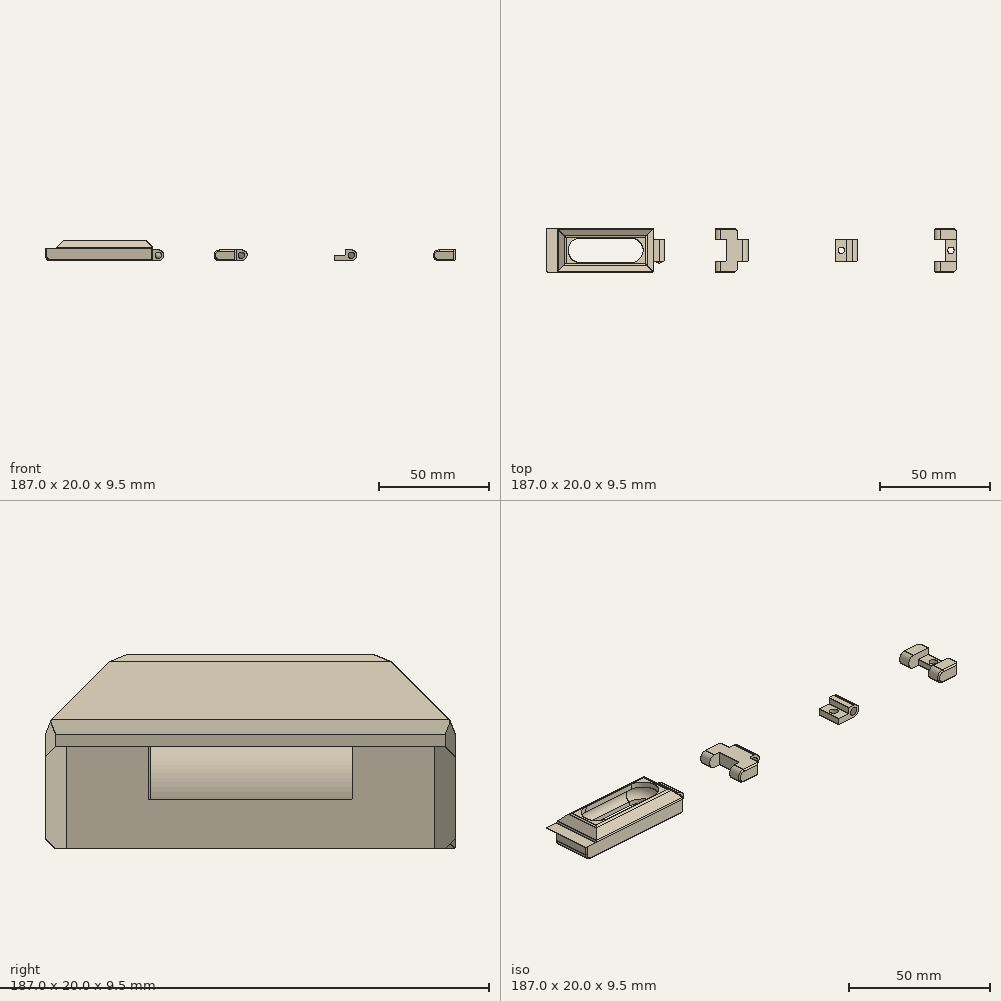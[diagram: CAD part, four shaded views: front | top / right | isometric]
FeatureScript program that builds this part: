
annotation { "Feature Type Name" : "Feature", "Feature Type Description" : "" }
export const myFeature = defineFeature(function(context is Context, id is Id, definition is map)
    precondition{}
    {
        {
            var Q0;
            Q0=qCreatedBy(makeId("Top.planeOp"),FACE);
            var sketch = newSketch(context, id + "F0", { "sketchPlane" : qUnion([Q0])});
            skLineSegment(sketch, "E0.bottom", {"start": v(-22, 10) * mm, "end": v(0, 10) * mm});
            skLineSegment(sketch, "E0.top", {"start": v(-22, -10) * mm, "end": v(0, -10) * mm});
            skLineSegment(sketch, "E0.left", {"start": v(-22, 10) * mm, "end": v(-22, -10) * mm});
            skLineSegment(sketch, "E0.right", {"start": v(0, 10) * mm, "end": v(0, -10) * mm});
            skSolve(sketch);
        }
        {
            var Q0;
            Q0=makeQuery(id+"F0.imprint","IMPRINT",FACE,{"disambiguationData":[TD([[makeQuery(id+"F0.imprint","IMPRINT",EDGE,{"derivedFrom":sQuery(id+"F0.wireOp",EDGE,"E0.bottom")}),-1.0]])]});
            extrude(context, id + "F1", {"entities" : qUnion([Q0]), "depth" : 10 * mm, "offsetDistance" : 25 * mm});
        }
        {
            var Q0;
            Q0=qCreatedBy(makeId("Right.planeOp"),FACE);
            var sketch = newSketch(context, id + "F2", { "sketchPlane" : qUnion([Q0])});
            skLineSegment(sketch, "E1.bottom", {"start": v(-5.6, 10) * mm, "end": v(5.6, 10) * mm});
            skLineSegment(sketch, "E1.left", {"start": v(-5.6, 10) * mm, "end": v(-5.5, 7.4) * mm});
            skLineSegment(sketch, "E1.right", {"start": v(5.6, 10) * mm, "end": v(5.7, 7.4) * mm});
            skLineSegment(sketch, "E2", {"start": v(-5.5, 1.4) * mm, "end": v(5.5, 1.4) * mm});
            skArc(sketch, "E3.trimOffspring", {"start": v(5.5, 1.4) * mm, "mid": v(8.5, 4.3) * mm, "end": v(5.7, 7.4) * mm});
            skArc(sketch, "E4.trimOffspring", {"start": v(-5.5, 7.4) * mm, "mid": v(-8.5, 4.4) * mm, "end": v(-5.5, 1.4) * mm});
            skSolve(sketch);
        }
        {
            var Q0;
            Q0=makeQuery(id+"F2.imprint","IMPRINT",FACE,{"disambiguationData":[TD([[makeQuery(id+"F2.imprint","IMPRINT",EDGE,{"derivedFrom":sQuery(id+"F2.wireOp",EDGE,"E1.bottom")}),-1.0]])]});
            extrude(context, id + "F3", {"entities" : qUnion([Q0]), "operationType" : NewBodyOperationType.REMOVE, "oppositeDirection" : true, "depth" : (37 / 2 - 7) * mm, "offsetDistance" : 25 * mm});
        }
        {
            var Q0;
            Q0=makeQuery(id+"F3.boolean.opBoolean","COPY",FACE,{"derivedFrom":makeQuery(id+"F3.opExtrude","CAP_FACE",FACE,{"disambiguationData":[OSD([sQuery(id+"F2.wireOp",EDGE,"E1.bottom"),sQuery(id+"F2.wireOp",EDGE,"E1.left"),sQuery(id+"F2.wireOp",EDGE,"E1.right"),sQuery(id+"F2.wireOp",EDGE,"E2"),sQuery(id+"F2.wireOp",EDGE,"E3.trimOffspring"),sQuery(id+"F2.wireOp",EDGE,"E4.trimOffspring")])],"isStart":false})});
            var sketch = newSketch(context, id + "F4", { "sketchPlane" : qUnion([Q0])});
            skLineSegment(sketch, "E5", {"start": v(0, 0) * mm, "end": v(0, 10) * mm});
            skSolve(sketch);
        }
        {
            var Q0;
            {var subQ0=makeQuery(id+"F3.boolean.opBoolean","COPY",EDGE,{"derivedFrom":makeQuery(id+"F3.opExtrude","CAP_EDGE",EDGE,{"disambiguationData":[OSD([sQuery(id+"F2.wireOp",EDGE,"E1.right")])],"isStart":false})});Q0=makeQuery(id+"F4.imprint","IMPRINT",FACE,{"disambiguationData":[TD([[makeQuery(id+"F4.imprint","IMPRINT",EDGE,{"derivedFrom":subQ0}),-1.0]])]});}
            var Q1;
            Q1=sQuery(id+"F4.wireOp",EDGE,"E5");
            revolve(context, id + "F5", {"operationType" : NewBodyOperationType.REMOVE, "surfaceOperationType" : NewSurfaceOperationType.NEW, "entities" : qUnion([Q0]), "axis" : qUnion([Q1]), "revolveType" : RevolveType.FULL, "oppositeDirection" : true});
        }
        {
            var Q0;
            Q0=makeQuery(id+"F1.opExtrude","SWEPT_BODY",BODY,{"disambiguationData":[OSD([sQuery(id+"F0.wireOp",EDGE,"E0.bottom"),sQuery(id+"F0.wireOp",EDGE,"E0.top"),sQuery(id+"F0.wireOp",EDGE,"E0.left"),sQuery(id+"F0.wireOp",EDGE,"E0.right")])]});
            var Q1;
            Q1=qCreatedBy(makeId("Right.planeOp"),FACE);
            mirror(context, id + "F6", {"operationType" : NewBodyOperationType.ADD, "entities" : qUnion([Q0]), "mirrorPlane" : qUnion([Q1])});
        }
        {
            var Q0;
            {var subQ0=makeQuery(id+"F1.opExtrude","CAP_FACE",FACE,{"disambiguationData":[OSD([sQuery(id+"F0.wireOp",EDGE,"E0.bottom"),sQuery(id+"F0.wireOp",EDGE,"E0.top"),sQuery(id+"F0.wireOp",EDGE,"E0.left"),sQuery(id+"F0.wireOp",EDGE,"E0.right")])],"isStart":true});Q0=makeQuery(id+"F6.boolean.opBoolean","MERGE",FACE,{"derivedFrom":[subQ0,makeQuery(id+"F6.opPattern","COPY",FACE,{"derivedFrom":subQ0,"instanceName":"1"})]});}
            var sketch = newSketch(context, id + "F7", { "sketchPlane" : qUnion([Q0])});
            skCircle(sketch, "E6", {"center": v(11.6, 0) * mm, "radius": 6.9 * mm});
            skCircle(sketch, "E7", {"center": v(-11.6, 0) * mm, "radius": 6.9 * mm});
            skLineSegment(sketch, "E8.bottom", {"start": v(-11.6, -6.9) * mm, "end": v(11.6, -6.9) * mm});
            skLineSegment(sketch, "E8.top", {"start": v(-11.6, 6.9) * mm, "end": v(11.6, 6.9) * mm});
            skLineSegment(sketch, "E8.left", {"start": v(-11.6, -6.9) * mm, "end": v(-11.6, 6.9) * mm});
            skLineSegment(sketch, "E8.right", {"start": v(11.6, -6.9) * mm, "end": v(11.6, 6.9) * mm});
            skSolve(sketch);
        }
        {
            var Q0;
            {var subQ0=sQuery(id+"F7.wireOp",EDGE,"E8.left");Q0=makeQuery(id+"F7.imprint","IMPRINT",FACE,{"disambiguationData":[TD([[makeQuery(id+"F7.imprint","IMPRINT",EDGE,{"derivedFrom":subQ0}),1.0]])]});}
            var Q1;
            {var subQ0=sQuery(id+"F7.wireOp",EDGE,"E8.left");Q1=makeQuery(id+"F7.imprint","IMPRINT",FACE,{"disambiguationData":[TD([[makeQuery(id+"F7.imprint","IMPRINT",EDGE,{"derivedFrom":subQ0}),-1.0]])]});}
            var Q2;
            {var subQ1=sQuery(id+"F7.wireOp",EDGE,"E8.bottom");Q2=makeQuery(id+"F7.imprint","IMPRINT",FACE,{"disambiguationData":[TD([[makeQuery(id+"F7.imprint","IMPRINT",EDGE,{"derivedFrom":subQ1}),1.0]])]});}
            var Q3;
            {var subQ0=sQuery(id+"F7.wireOp",EDGE,"E8.right");Q3=makeQuery(id+"F7.imprint","IMPRINT",FACE,{"disambiguationData":[TD([[makeQuery(id+"F7.imprint","IMPRINT",EDGE,{"derivedFrom":subQ0}),1.0]])]});}
            var Q4;
            {var subQ0=sQuery(id+"F7.wireOp",EDGE,"E8.right");Q4=makeQuery(id+"F7.imprint","IMPRINT",FACE,{"disambiguationData":[TD([[makeQuery(id+"F7.imprint","IMPRINT",EDGE,{"derivedFrom":subQ0}),-1.0]])]});}
            extrude(context, id + "F8", {"entities" : qUnion([Q0, Q1, Q2, Q3, Q4]), "operationType" : NewBodyOperationType.REMOVE, "oppositeDirection" : true, "depth" : 3 * mm, "offsetDistance" : 25 * mm});
        }
        {
            var Q0;
            Q0=makeQuery(id+"F1.opExtrude","CAP_EDGE",EDGE,{"disambiguationData":[OSD([sQuery(id+"F0.wireOp",EDGE,"E0.left")])],"isStart":false});
            var Q1;
            {var subQ0=makeQuery(id+"F1.opExtrude","CAP_EDGE",EDGE,{"disambiguationData":[OSD([sQuery(id+"F0.wireOp",EDGE,"E0.bottom")])],"isStart":false});Q1=makeQuery(id+"F6.boolean.opBoolean","MERGE",EDGE,{"derivedFrom":[subQ0,makeQuery(id+"F6.opPattern","COPY",EDGE,{"derivedFrom":subQ0,"instanceName":"1"})]});}
            var Q2;
            {var subQ0=makeQuery(id+"F1.opExtrude","CAP_EDGE",EDGE,{"disambiguationData":[OSD([sQuery(id+"F0.wireOp",EDGE,"E0.top")])],"isStart":false});Q2=makeQuery(id+"F6.boolean.opBoolean","MERGE",EDGE,{"derivedFrom":[subQ0,makeQuery(id+"F6.opPattern","COPY",EDGE,{"derivedFrom":subQ0,"instanceName":"1"})]});}
            var Q3;
            Q3=makeQuery(id+"F6.opPattern","COPY",EDGE,{"derivedFrom":makeQuery(id+"F1.opExtrude","CAP_EDGE",EDGE,{"disambiguationData":[OSD([sQuery(id+"F0.wireOp",EDGE,"E0.left")])],"isStart":false}),"instanceName":"1"});
            chamfer(context, id + "F9", {"entities" : qUnion([Q0, Q1, Q2, Q3]), "width" : 4 * mm, "tangentPropagation" : true});
        }
        {
            var Q0;
            {var subQ0=sQuery(id+"F0.wireOp",EDGE,"E0.bottom");var subQ1=makeQuery(id+"F1.opExtrude","CAP_FACE",FACE,{"disambiguationData":[OSD([subQ0,sQuery(id+"F0.wireOp",EDGE,"E0.top"),sQuery(id+"F0.wireOp",EDGE,"E0.left"),sQuery(id+"F0.wireOp",EDGE,"E0.right")])],"isStart":false});var subQ2=makeQuery(id+"F1.opExtrude","CAP_EDGE",EDGE,{"disambiguationData":[OSD([subQ0])],"isStart":false});Q0=makeQuery(id+"F9.opChamfer","BLEND_EDGE",EDGE,{"blendedFrom":[makeQuery(id+"F6.boolean.opBoolean","MERGE",EDGE,{"derivedFrom":[subQ2,makeQuery(id+"F6.opPattern","COPY",EDGE,{"derivedFrom":subQ2,"instanceName":"1"})]}),makeQuery(id+"F6.boolean.opBoolean","MERGE",FACE,{"derivedFrom":[subQ1,makeQuery(id+"F6.opPattern","COPY",FACE,{"derivedFrom":subQ1,"instanceName":"1"})]})],"blendedInto":[makeQuery(id+"F6.boolean.opBoolean","MERGE",FACE,{"derivedFrom":[subQ1,makeQuery(id+"F6.opPattern","COPY",FACE,{"derivedFrom":subQ1,"instanceName":"1"})]})]});}
            var Q1;
            {var subQ0=sQuery(id+"F0.wireOp",EDGE,"E0.left");var subQ1=makeQuery(id+"F1.opExtrude","CAP_FACE",FACE,{"disambiguationData":[OSD([sQuery(id+"F0.wireOp",EDGE,"E0.bottom"),sQuery(id+"F0.wireOp",EDGE,"E0.top"),subQ0,sQuery(id+"F0.wireOp",EDGE,"E0.right")])],"isStart":false});Q1=makeQuery(id+"F9.opChamfer","BLEND_EDGE",EDGE,{"blendedFrom":[makeQuery(id+"F1.opExtrude","CAP_EDGE",EDGE,{"disambiguationData":[OSD([subQ0])],"isStart":false}),makeQuery(id+"F6.boolean.opBoolean","MERGE",FACE,{"derivedFrom":[subQ1,makeQuery(id+"F6.opPattern","COPY",FACE,{"derivedFrom":subQ1,"instanceName":"1"})]})],"blendedInto":[makeQuery(id+"F6.boolean.opBoolean","MERGE",FACE,{"derivedFrom":[subQ1,makeQuery(id+"F6.opPattern","COPY",FACE,{"derivedFrom":subQ1,"instanceName":"1"})]})]});}
            var Q2;
            {var subQ0=sQuery(id+"F0.wireOp",EDGE,"E0.top");var subQ1=makeQuery(id+"F1.opExtrude","CAP_FACE",FACE,{"disambiguationData":[OSD([sQuery(id+"F0.wireOp",EDGE,"E0.bottom"),subQ0,sQuery(id+"F0.wireOp",EDGE,"E0.left"),sQuery(id+"F0.wireOp",EDGE,"E0.right")])],"isStart":false});var subQ2=makeQuery(id+"F1.opExtrude","CAP_EDGE",EDGE,{"disambiguationData":[OSD([subQ0])],"isStart":false});Q2=makeQuery(id+"F9.opChamfer","BLEND_EDGE",EDGE,{"blendedFrom":[makeQuery(id+"F6.boolean.opBoolean","MERGE",EDGE,{"derivedFrom":[subQ2,makeQuery(id+"F6.opPattern","COPY",EDGE,{"derivedFrom":subQ2,"instanceName":"1"})]}),makeQuery(id+"F6.boolean.opBoolean","MERGE",FACE,{"derivedFrom":[subQ1,makeQuery(id+"F6.opPattern","COPY",FACE,{"derivedFrom":subQ1,"instanceName":"1"})]})],"blendedInto":[makeQuery(id+"F6.boolean.opBoolean","MERGE",FACE,{"derivedFrom":[subQ1,makeQuery(id+"F6.opPattern","COPY",FACE,{"derivedFrom":subQ1,"instanceName":"1"})]})]});}
            var Q3;
            {var subQ0=sQuery(id+"F0.wireOp",EDGE,"E0.left");var subQ1=makeQuery(id+"F1.opExtrude","CAP_FACE",FACE,{"disambiguationData":[OSD([sQuery(id+"F0.wireOp",EDGE,"E0.bottom"),sQuery(id+"F0.wireOp",EDGE,"E0.top"),subQ0,sQuery(id+"F0.wireOp",EDGE,"E0.right")])],"isStart":false});Q3=makeQuery(id+"F9.opChamfer","BLEND_EDGE",EDGE,{"blendedFrom":[makeQuery(id+"F6.opPattern","COPY",EDGE,{"derivedFrom":makeQuery(id+"F1.opExtrude","CAP_EDGE",EDGE,{"disambiguationData":[OSD([subQ0])],"isStart":false}),"instanceName":"1"}),makeQuery(id+"F6.boolean.opBoolean","MERGE",FACE,{"derivedFrom":[subQ1,makeQuery(id+"F6.opPattern","COPY",FACE,{"derivedFrom":subQ1,"instanceName":"1"})]})],"blendedInto":[makeQuery(id+"F6.boolean.opBoolean","MERGE",FACE,{"derivedFrom":[subQ1,makeQuery(id+"F6.opPattern","COPY",FACE,{"derivedFrom":subQ1,"instanceName":"1"})]})]});}
            chamfer(context, id + "F10", {"entities" : qUnion([Q0, Q1, Q2, Q3]), "width" : 3 * mm, "tangentPropagation" : true});
        }
        {
            var Q0;
            {var subQ0=sQuery(id+"F0.wireOp",EDGE,"E0.left");Q0=makeQuery(id+"F9.opChamfer","BLEND_EDGE",EDGE,{"blendedFrom":[makeQuery(id+"F1.opExtrude","CAP_EDGE",EDGE,{"disambiguationData":[OSD([subQ0])],"isStart":false}),makeQuery(id+"F1.opExtrude","SWEPT_FACE",FACE,{"disambiguationData":[OSD([subQ0])]})],"blendedInto":[makeQuery(id+"F1.opExtrude","SWEPT_FACE",FACE,{"disambiguationData":[OSD([subQ0])]})]});}
            var Q1;
            {var subQ0=sQuery(id+"F0.wireOp",EDGE,"E0.bottom");var subQ1=makeQuery(id+"F1.opExtrude","SWEPT_FACE",FACE,{"disambiguationData":[OSD([subQ0])]});var subQ2=makeQuery(id+"F1.opExtrude","CAP_EDGE",EDGE,{"disambiguationData":[OSD([subQ0])],"isStart":false});Q1=makeQuery(id+"F9.opChamfer","BLEND_EDGE",EDGE,{"blendedFrom":[makeQuery(id+"F6.boolean.opBoolean","MERGE",EDGE,{"derivedFrom":[subQ2,makeQuery(id+"F6.opPattern","COPY",EDGE,{"derivedFrom":subQ2,"instanceName":"1"})]}),makeQuery(id+"F6.boolean.opBoolean","MERGE",FACE,{"derivedFrom":[subQ1,makeQuery(id+"F6.opPattern","COPY",FACE,{"derivedFrom":subQ1,"instanceName":"1"})]})],"blendedInto":[makeQuery(id+"F6.boolean.opBoolean","MERGE",FACE,{"derivedFrom":[subQ1,makeQuery(id+"F6.opPattern","COPY",FACE,{"derivedFrom":subQ1,"instanceName":"1"})]})]});}
            var Q2;
            {var subQ0=sQuery(id+"F0.wireOp",EDGE,"E0.top");var subQ1=makeQuery(id+"F1.opExtrude","SWEPT_FACE",FACE,{"disambiguationData":[OSD([subQ0])]});var subQ2=makeQuery(id+"F1.opExtrude","CAP_EDGE",EDGE,{"disambiguationData":[OSD([subQ0])],"isStart":false});Q2=makeQuery(id+"F9.opChamfer","BLEND_EDGE",EDGE,{"blendedFrom":[makeQuery(id+"F6.boolean.opBoolean","MERGE",EDGE,{"derivedFrom":[subQ2,makeQuery(id+"F6.opPattern","COPY",EDGE,{"derivedFrom":subQ2,"instanceName":"1"})]}),makeQuery(id+"F6.boolean.opBoolean","MERGE",FACE,{"derivedFrom":[subQ1,makeQuery(id+"F6.opPattern","COPY",FACE,{"derivedFrom":subQ1,"instanceName":"1"})]})],"blendedInto":[makeQuery(id+"F6.boolean.opBoolean","MERGE",FACE,{"derivedFrom":[subQ1,makeQuery(id+"F6.opPattern","COPY",FACE,{"derivedFrom":subQ1,"instanceName":"1"})]})]});}
            var Q3;
            {var subQ0=sQuery(id+"F0.wireOp",EDGE,"E0.left");Q3=makeQuery(id+"F9.opChamfer","BLEND_EDGE",EDGE,{"blendedFrom":[makeQuery(id+"F6.opPattern","COPY",EDGE,{"derivedFrom":makeQuery(id+"F1.opExtrude","CAP_EDGE",EDGE,{"disambiguationData":[OSD([subQ0])],"isStart":false}),"instanceName":"1"}),makeQuery(id+"F6.opPattern","COPY",FACE,{"derivedFrom":makeQuery(id+"F1.opExtrude","SWEPT_FACE",FACE,{"disambiguationData":[OSD([subQ0])]}),"instanceName":"1"})],"blendedInto":[makeQuery(id+"F6.opPattern","COPY",FACE,{"derivedFrom":makeQuery(id+"F1.opExtrude","SWEPT_FACE",FACE,{"disambiguationData":[OSD([subQ0])]}),"instanceName":"1"})]});}
            chamfer(context, id + "F11", {"entities" : qUnion([Q0, Q1, Q2, Q3]), "width" : 1 * mm, "tangentPropagation" : true});
        }
        {
            var Q0;
            Q0=makeQuery(id+"F1.opExtrude","SWEPT_FACE",FACE,{"disambiguationData":[OSD([sQuery(id+"F0.wireOp",EDGE,"E0.left")])]});
            var sketch = newSketch(context, id + "F12", { "sketchPlane" : qUnion([Q0])});
            skLineSegment(sketch, "E9.bottom", {"start": v(-10, 5) * mm, "end": v(-5, 5) * mm});
            skLineSegment(sketch, "E9.top", {"start": v(-10, 0) * mm, "end": v(-5, 0) * mm});
            skLineSegment(sketch, "E9.left", {"start": v(-10, 5) * mm, "end": v(-10, 0) * mm});
            skLineSegment(sketch, "E9.right", {"start": v(-5, 5) * mm, "end": v(-5, 0) * mm});
            skLineSegment(sketch, "E10.bottom", {"start": v(10, 5) * mm, "end": v(5, 5) * mm});
            skLineSegment(sketch, "E10.top", {"start": v(10, 0) * mm, "end": v(5, 0) * mm});
            skLineSegment(sketch, "E10.left", {"start": v(10, 5) * mm, "end": v(10, 0) * mm});
            skLineSegment(sketch, "E10.right", {"start": v(5, 5) * mm, "end": v(5, 0) * mm});
            skSolve(sketch);
        }
        {
            var Q0;
            Q0=makeQuery(id+"F12.imprint","IMPRINT",FACE,{"disambiguationData":[TD([[makeQuery(id+"F12.imprint","IMPRINT",EDGE,{"derivedFrom":sQuery(id+"F12.wireOp",EDGE,"E9.bottom")}),1.0]])]});
            var Q1;
            Q1=makeQuery(id+"F12.imprint","IMPRINT",FACE,{"disambiguationData":[TD([[makeQuery(id+"F12.imprint","IMPRINT",EDGE,{"derivedFrom":sQuery(id+"F12.wireOp",EDGE,"E10.bottom")}),1.0]])]});
            extrude(context, id + "F13", {"entities" : qUnion([Q0, Q1]), "operationType" : NewBodyOperationType.ADD, "depth" : 5 * mm, "offsetDistance" : 25 * mm});
        }
        {
            var Q0;
            Q0=makeQuery(id+"F6.opPattern","COPY",FACE,{"derivedFrom":makeQuery(id+"F1.opExtrude","SWEPT_FACE",FACE,{"disambiguationData":[OSD([sQuery(id+"F0.wireOp",EDGE,"E0.left")])]}),"instanceName":"1"});
            var sketch = newSketch(context, id + "F14", { "sketchPlane" : qUnion([Q0])});
            skLineSegment(sketch, "E11.bottom", {"start": v(-5, 0) * mm, "end": v(5, 0) * mm});
            skLineSegment(sketch, "E11.top", {"start": v(-5, 5) * mm, "end": v(5, 5) * mm});
            skLineSegment(sketch, "E11.left", {"start": v(-5, 0) * mm, "end": v(-5, 5) * mm});
            skLineSegment(sketch, "E11.right", {"start": v(5, 0) * mm, "end": v(5, 5) * mm});
            skSolve(sketch);
        }
        {
            var Q0;
            Q0=makeQuery(id+"F14.imprint","IMPRINT",FACE,{"disambiguationData":[TD([[makeQuery(id+"F14.imprint","IMPRINT",EDGE,{"derivedFrom":sQuery(id+"F14.wireOp",EDGE,"E11.bottom")}),-1.0]])]});
            extrude(context, id + "F15", {"entities" : qUnion([Q0]), "operationType" : NewBodyOperationType.ADD, "depth" : 5 * mm, "offsetDistance" : 25 * mm});
        }
        {
            var Q0;
            Q0=makeQuery(id+"F13.opExtrude","CAP_EDGE",EDGE,{"disambiguationData":[OSD([sQuery(id+"F12.wireOp",EDGE,"E9.bottom")])],"isStart":false});
            var Q1;
            Q1=makeQuery(id+"F13.opExtrude","CAP_EDGE",EDGE,{"disambiguationData":[OSD([sQuery(id+"F12.wireOp",EDGE,"E9.top")])],"isStart":false});
            var Q2;
            Q2=makeQuery(id+"F13.opExtrude","CAP_EDGE",EDGE,{"disambiguationData":[OSD([sQuery(id+"F12.wireOp",EDGE,"E10.bottom")])],"isStart":false});
            var Q3;
            Q3=makeQuery(id+"F13.opExtrude","CAP_EDGE",EDGE,{"disambiguationData":[OSD([sQuery(id+"F12.wireOp",EDGE,"E10.top")])],"isStart":false});
            var Q4;
            Q4=makeQuery(id+"F15.opExtrude","CAP_EDGE",EDGE,{"disambiguationData":[OSD([sQuery(id+"F14.wireOp",EDGE,"E11.top")])],"isStart":false});
            var Q5;
            Q5=makeQuery(id+"F15.opExtrude","CAP_EDGE",EDGE,{"disambiguationData":[OSD([sQuery(id+"F14.wireOp",EDGE,"E11.bottom")])],"isStart":false});
            fillet(context, id + "F16", {"entities" : qUnion([Q0, Q1, Q2, Q3, Q4, Q5]), "radius" : 2.5 * mm, "tangentPropagation" : true, "allowEdgeOverflow" : false});
        }
        {
            var Q0;
            Q0=qCreatedBy(makeId("Top.planeOp"),FACE);
            cPlane(context, id + "F17", {"entities" : qUnion([Q0]), "cplaneType" : CPlaneType.OFFSET, "offset" : 10 * mm, "width" : 150 * mm, "height" : 150 * mm});
        }
        {
            var Q0;
            Q0=qCreatedBy(id+"F17.planeOp",FACE);
            var sketch = newSketch(context, id + "F18", { "sketchPlane" : qUnion([Q0])});
            skLineSegment(sketch, "E12.bottom", {"start": v(22.66, 7.24) * mm, "end": v(-22.46, 7.24) * mm});
            skLineSegment(sketch, "E12.top", {"start": v(22.66, -7.34) * mm, "end": v(-22.46, -7.34) * mm});
            skLineSegment(sketch, "E12.left", {"start": v(22.66, 7.24) * mm, "end": v(22.66, -7.34) * mm});
            skLineSegment(sketch, "E12.right", {"start": v(-22.46, 7.24) * mm, "end": v(-22.46, -7.34) * mm});
            skSolve(sketch);
        }
        {
            var Q0;
            Q0=makeQuery(id+"F18.imprint","IMPRINT",FACE,{"disambiguationData":[TD([[makeQuery(id+"F18.imprint","IMPRINT",EDGE,{"derivedFrom":sQuery(id+"F18.wireOp",EDGE,"E12.bottom")}),1.0]])]});
            extrude(context, id + "F19", {"entities" : qUnion([Q0]), "operationType" : NewBodyOperationType.REMOVE, "oppositeDirection" : true, "depth" : 0.5 * mm, "offsetDistance" : 25 * mm});
        }
        {
            var Q0;
            Q0=qCreatedBy(makeId("Right.planeOp"),FACE);
            cPlane(context, id + "F20", {"entities" : qUnion([Q0]), "cplaneType" : CPlaneType.OFFSET, "offset" : 50 * mm, "width" : 150 * mm, "height" : 150 * mm});
        }
        {
            var Q0;
            Q0=qCreatedBy(id+"F20.planeOp",FACE);
            var sketch = newSketch(context, id + "F21", { "sketchPlane" : qUnion([Q0])});
            skLineSegment(sketch, "E13.bottom", {"start": v(-10, 0) * mm, "end": v(10, 0) * mm});
            skLineSegment(sketch, "E13.top", {"start": v(-10, 5) * mm, "end": v(10, 5) * mm});
            skLineSegment(sketch, "E13.left", {"start": v(-10, 0) * mm, "end": v(-10, 5) * mm});
            skLineSegment(sketch, "E13.right", {"start": v(10, 0) * mm, "end": v(10, 5) * mm});
            skSolve(sketch);
        }
        {
            var Q0;
            Q0=makeQuery(id+"F21.imprint","IMPRINT",FACE,{"disambiguationData":[TD([[makeQuery(id+"F21.imprint","IMPRINT",EDGE,{"derivedFrom":sQuery(id+"F21.wireOp",EDGE,"E13.bottom")}),1.0]])]});
            extrude(context, id + "F22", {"entities" : qUnion([Q0]), "depth" : 10 * mm, "offsetDistance" : 25 * mm});
        }
        {
            var Q0;
            Q0=makeQuery(id+"F22.opExtrude","CAP_FACE",FACE,{"disambiguationData":[OSD([sQuery(id+"F21.wireOp",EDGE,"E13.bottom"),sQuery(id+"F21.wireOp",EDGE,"E13.top"),sQuery(id+"F21.wireOp",EDGE,"E13.left"),sQuery(id+"F21.wireOp",EDGE,"E13.right")])],"isStart":false});
            var sketch = newSketch(context, id + "F23", { "sketchPlane" : qUnion([Q0])});
            skLineSegment(sketch, "E14.bottom", {"start": v(-5, 0) * mm, "end": v(5, 0) * mm});
            skLineSegment(sketch, "E14.top", {"start": v(-5, 5) * mm, "end": v(5, 5) * mm});
            skLineSegment(sketch, "E14.left", {"start": v(-5, 0) * mm, "end": v(-5, 5) * mm});
            skLineSegment(sketch, "E14.right", {"start": v(5, 0) * mm, "end": v(5, 5) * mm});
            skSolve(sketch);
        }
        {
            var Q0;
            Q0=makeQuery(id+"F23.imprint","IMPRINT",FACE,{"disambiguationData":[TD([[makeQuery(id+"F23.imprint","IMPRINT",EDGE,{"derivedFrom":sQuery(id+"F23.wireOp",EDGE,"E14.bottom")}),1.0]])]});
            extrude(context, id + "F24", {"entities" : qUnion([Q0]), "operationType" : NewBodyOperationType.ADD, "depth" : 5 * mm, "offsetDistance" : 25 * mm});
        }
        {
            var Q0;
            Q0=makeQuery(id+"F22.opExtrude","CAP_FACE",FACE,{"disambiguationData":[OSD([sQuery(id+"F21.wireOp",EDGE,"E13.bottom"),sQuery(id+"F21.wireOp",EDGE,"E13.top"),sQuery(id+"F21.wireOp",EDGE,"E13.left"),sQuery(id+"F21.wireOp",EDGE,"E13.right")])],"isStart":true});
            var sketch = newSketch(context, id + "F25", { "sketchPlane" : qUnion([Q0])});
            skLineSegment(sketch, "E15.bottom", {"start": v(-5, 0) * mm, "end": v(5, 0) * mm});
            skLineSegment(sketch, "E15.top", {"start": v(-5, 5) * mm, "end": v(5, 5) * mm});
            skLineSegment(sketch, "E15.left", {"start": v(-5, 0) * mm, "end": v(-5, 5) * mm});
            skLineSegment(sketch, "E15.right", {"start": v(5, 0) * mm, "end": v(5, 5) * mm});
            skSolve(sketch);
        }
        {
            var Q0;
            Q0=makeQuery(id+"F25.imprint","IMPRINT",FACE,{"disambiguationData":[TD([[makeQuery(id+"F25.imprint","IMPRINT",EDGE,{"derivedFrom":sQuery(id+"F25.wireOp",EDGE,"E15.bottom")}),-1.0]])]});
            extrude(context, id + "F26", {"entities" : qUnion([Q0]), "operationType" : NewBodyOperationType.REMOVE, "oppositeDirection" : true, "depth" : 5 * mm, "offsetDistance" : 25 * mm});
        }
        {
            var Q0;
            {var subQ0=sQuery(id+"F21.wireOp",EDGE,"E13.right");var subQ1=sQuery(id+"F21.wireOp",EDGE,"E13.top");Q0=makeQuery(id+"F26.boolean.opBoolean","SPLIT",EDGE,{"disambiguationData":[TD([makeQuery(id+"F22.opExtrude","SWEPT_FACE",FACE,{"disambiguationData":[OSD([subQ0])]})])],"derivedFrom":makeQuery(id+"F22.opExtrude","CAP_EDGE",EDGE,{"disambiguationData":[OSD([subQ1])],"isStart":true})});}
            var Q1;
            {var subQ0=sQuery(id+"F21.wireOp",EDGE,"E13.right");var subQ1=sQuery(id+"F21.wireOp",EDGE,"E13.bottom");Q1=makeQuery(id+"F26.boolean.opBoolean","SPLIT",EDGE,{"disambiguationData":[TD([makeQuery(id+"F22.opExtrude","SWEPT_FACE",FACE,{"disambiguationData":[OSD([subQ0])]})])],"derivedFrom":makeQuery(id+"F22.opExtrude","CAP_EDGE",EDGE,{"disambiguationData":[OSD([subQ1])],"isStart":true})});}
            var Q2;
            {var subQ0=sQuery(id+"F21.wireOp",EDGE,"E13.left");var subQ1=sQuery(id+"F21.wireOp",EDGE,"E13.top");Q2=makeQuery(id+"F26.boolean.opBoolean","SPLIT",EDGE,{"disambiguationData":[TD([makeQuery(id+"F22.opExtrude","SWEPT_FACE",FACE,{"disambiguationData":[OSD([subQ0])]})])],"derivedFrom":makeQuery(id+"F22.opExtrude","CAP_EDGE",EDGE,{"disambiguationData":[OSD([subQ1])],"isStart":true})});}
            var Q3;
            {var subQ0=sQuery(id+"F21.wireOp",EDGE,"E13.left");var subQ1=sQuery(id+"F21.wireOp",EDGE,"E13.bottom");Q3=makeQuery(id+"F26.boolean.opBoolean","SPLIT",EDGE,{"disambiguationData":[TD([makeQuery(id+"F22.opExtrude","SWEPT_FACE",FACE,{"disambiguationData":[OSD([subQ0])]})])],"derivedFrom":makeQuery(id+"F22.opExtrude","CAP_EDGE",EDGE,{"disambiguationData":[OSD([subQ1])],"isStart":true})});}
            var Q4;
            Q4=makeQuery(id+"F24.opExtrude","CAP_EDGE",EDGE,{"disambiguationData":[OSD([sQuery(id+"F23.wireOp",EDGE,"E14.top")])],"isStart":false});
            var Q5;
            Q5=makeQuery(id+"F24.opExtrude","CAP_EDGE",EDGE,{"disambiguationData":[OSD([sQuery(id+"F23.wireOp",EDGE,"E14.bottom")])],"isStart":false});
            fillet(context, id + "F27", {"entities" : qUnion([Q0, Q1, Q2, Q3, Q4, Q5]), "radius" : 2.5 * mm, "tangentPropagation" : true, "allowEdgeOverflow" : false});
        }
        {
            var Q0;
            Q0=makeQuery(id+"F22.opExtrude","CAP_EDGE",EDGE,{"disambiguationData":[OSD([sQuery(id+"F21.wireOp",EDGE,"E13.left")])],"isStart":false});
            var Q1;
            Q1=makeQuery(id+"F22.opExtrude","CAP_EDGE",EDGE,{"disambiguationData":[OSD([sQuery(id+"F21.wireOp",EDGE,"E13.right")])],"isStart":false});
            chamfer(context, id + "F28", {"entities" : qUnion([Q0, Q1]), "width" : 1 * mm, "tangentPropagation" : true});
        }
        {
            var Q0;
            Q0=makeQuery(id+"F24.opExtrude","SWEPT_FACE",FACE,{"disambiguationData":[OSD([sQuery(id+"F23.wireOp",EDGE,"E14.left")])]});
            var Q1;
            Q1=makeQuery(id+"F24.opExtrude","SWEPT_FACE",FACE,{"disambiguationData":[OSD([sQuery(id+"F23.wireOp",EDGE,"E14.right")])]});
            extrude(context, id + "F29", {"entities" : qUnion([Q0, Q1]), "operationType" : NewBodyOperationType.REMOVE, "oppositeDirection" : true, "depth" : 0.1 * mm, "offsetDistance" : 25 * mm});
        }
        {
            var Q0;
            Q0=makeQuery(id+"F29.boolean.opBoolean","COPY",FACE,{"derivedFrom":makeQuery(id+"F29.opExtrude","CAP_FACE",FACE,{"disambiguationData":[OSD([sQuery(id+"F23.wireOp",EDGE,"E14.left")])],"isStart":false})});
            var sketch = newSketch(context, id + "F30", { "sketchPlane" : qUnion([Q0])});
            skArc(sketch, "E16", {"start": v(62.5, 1.5) * mm, "mid": v(63.5, 2.5) * mm, "end": v(62.5, 3.5) * mm});
            skLineSegment(sketch, "E17", {"start": v(62.5, 2.5) * mm, "end": v(62.5, 3.5) * mm});
            skLineSegment(sketch, "E18", {"start": v(62.5, 2.5) * mm, "end": v(62.5, 1.5) * mm});
            skSolve(sketch);
        }
        {
            var Q0;
            Q0=qCreatedBy(makeId("Front.planeOp"),FACE);
            cPlane(context, id + "F31", {"entities" : qUnion([Q0]), "cplaneType" : CPlaneType.OFFSET, "offset" : 4 * mm, "width" : 150 * mm, "height" : 150 * mm});
        }
        {
            var Q0;
            Q0=qCreatedBy(id+"F31.planeOp",FACE);
            var sketch = newSketch(context, id + "F32", { "sketchPlane" : qUnion([Q0])});
            skArc(sketch, "E19", {"start": v(62.5, 0.75) * mm, "mid": v(64.25, 2.5) * mm, "end": v(62.5, 4.25) * mm});
            skLineSegment(sketch, "E20", {"start": v(62.5, 4.25) * mm, "end": v(62.5, 0.75) * mm});
            skSolve(sketch);
        }
        {
            var Q0;
            Q0 = qSketchRegion(id + "F32", true);
            var Q1;
            Q1=sQuery(id+"F32.wireOp",EDGE,"E20");
            revolve(context, id + "F33", {"operationType" : NewBodyOperationType.ADD, "surfaceOperationType" : NewSurfaceOperationType.NEW, "entities" : qUnion([Q0]), "axis" : qUnion([Q1]), "revolveType" : RevolveType.FULL});
        }
        {
            var Q0;
            Q0=qCreatedBy(id+"F31.planeOp",FACE);
            var sketch = newSketch(context, id + "F34", { "sketchPlane" : qUnion([Q0])});
            skArc(sketch, "E21", {"start": v(52.5, 4.25) * mm, "mid": v(50.75, 2.5) * mm, "end": v(52.5, 0.75) * mm});
            skLineSegment(sketch, "E22", {"start": v(52.5, 4.25) * mm, "end": v(52.5, 0.75) * mm});
            skSolve(sketch);
        }
        {
            var Q0;
            Q0=makeQuery(id+"F34.imprint","IMPRINT",FACE,{"disambiguationData":[TD([[makeQuery(id+"F34.imprint","IMPRINT",EDGE,{"derivedFrom":sQuery(id+"F34.wireOp",EDGE,"E21")}),1.0]])]});
            var Q1;
            Q1=sQuery(id+"F34.wireOp",EDGE,"E22");
            revolve(context, id + "F35", {"operationType" : NewBodyOperationType.REMOVE, "surfaceOperationType" : NewSurfaceOperationType.NEW, "entities" : qUnion([Q0]), "axis" : qUnion([Q1]), "revolveType" : RevolveType.FULL, "oppositeDirection" : true});
        }
        {
            var Q0;
            Q0=makeQuery(id+"F22.opExtrude","SWEPT_EDGE",EDGE,{"disambiguationData":[OSD([sQuery(id+"F21.wireOp",EDGE,"E13.top"),sQuery(id+"F21.wireOp",EDGE,"E13.left")])]});
            var Q1;
            Q1=makeQuery(id+"F22.opExtrude","SWEPT_EDGE",EDGE,{"disambiguationData":[OSD([sQuery(id+"F21.wireOp",EDGE,"E13.top"),sQuery(id+"F21.wireOp",EDGE,"E13.right")])]});
            var Q2;
            Q2=makeQuery(id+"F26.boolean.opBoolean","COPY",EDGE,{"derivedFrom":makeQuery(id+"F26.opExtrude","CAP_EDGE",EDGE,{"disambiguationData":[OSD([sQuery(id+"F25.wireOp",EDGE,"E15.bottom")])],"isStart":false})});
            var Q3;
            Q3=makeQuery(id+"F26.boolean.opBoolean","COPY",EDGE,{"derivedFrom":makeQuery(id+"F26.opExtrude","CAP_EDGE",EDGE,{"disambiguationData":[OSD([sQuery(id+"F25.wireOp",EDGE,"E15.top")])],"isStart":false})});
            chamfer(context, id + "F36", {"entities" : qUnion([Q0, Q1, Q2, Q3]), "width" : 0.5 * mm, "tangentPropagation" : true});
        }
        {
            var Q0;
            Q0=qCreatedBy(id+"F31.planeOp",FACE);
            var sketch = newSketch(context, id + "F37", { "sketchPlane" : qUnion([Q0])});
            skArc(sketch, "E23", {"start": v(24.5, 0.75) * mm, "mid": v(26.25, 2.5) * mm, "end": v(24.5, 4.25) * mm});
            skLineSegment(sketch, "E24", {"start": v(24.5, 2.5) * mm, "end": v(24.5, 4.25) * mm});
            skLineSegment(sketch, "E25", {"start": v(24.5, 2.5) * mm, "end": v(24.5, 0.75) * mm});
            skArc(sketch, "E26", {"start": v(-24.5, 4.25) * mm, "mid": v(-26.25, 2.5) * mm, "end": v(-24.5, 0.75) * mm});
            skLineSegment(sketch, "E27", {"start": v(-24.5, 0.75) * mm, "end": v(-24.5, 4.25) * mm});
            skSolve(sketch);
        }
        {
            var Q0;
            Q0=makeQuery(id+"F15.opExtrude","SWEPT_FACE",FACE,{"disambiguationData":[OSD([sQuery(id+"F14.wireOp",EDGE,"E11.left")])]});
            var Q1;
            Q1=makeQuery(id+"F15.opExtrude","SWEPT_FACE",FACE,{"disambiguationData":[OSD([sQuery(id+"F14.wireOp",EDGE,"E11.right")])]});
            extrude(context, id + "F38", {"entities" : qUnion([Q0, Q1]), "operationType" : NewBodyOperationType.REMOVE, "oppositeDirection" : true, "depth" : 0.1 * mm, "offsetDistance" : 25 * mm});
        }
        {
            var Q0;
            Q0=makeQuery(id+"F37.imprint","IMPRINT",FACE,{"disambiguationData":[TD([[makeQuery(id+"F37.imprint","IMPRINT",EDGE,{"derivedFrom":sQuery(id+"F37.wireOp",EDGE,"E23")}),1.0]])]});
            var Q1;
            Q1=sQuery(id+"F37.wireOp",EDGE,"E24");
            revolve(context, id + "F39", {"operationType" : NewBodyOperationType.ADD, "surfaceOperationType" : NewSurfaceOperationType.NEW, "entities" : qUnion([Q0]), "axis" : qUnion([Q1]), "revolveType" : RevolveType.FULL});
        }
        {
            var Q0;
            Q0=makeQuery(id+"F37.imprint","IMPRINT",FACE,{"disambiguationData":[TD([[makeQuery(id+"F37.imprint","IMPRINT",EDGE,{"derivedFrom":sQuery(id+"F37.wireOp",EDGE,"E26")}),1.0]])]});
            var Q1;
            Q1=sQuery(id+"F37.wireOp",EDGE,"E27");
            revolve(context, id + "F40", {"operationType" : NewBodyOperationType.REMOVE, "surfaceOperationType" : NewSurfaceOperationType.NEW, "entities" : qUnion([Q0]), "axis" : qUnion([Q1]), "revolveType" : RevolveType.FULL, "oppositeDirection" : true});
        }
        {
            var Q0;
            {var subQ0=makeQuery(id+"F1.opExtrude","CAP_EDGE",EDGE,{"disambiguationData":[OSD([sQuery(id+"F0.wireOp",EDGE,"E0.top")])],"isStart":true});Q0=makeQuery(id+"F13.boolean.opBoolean","MERGE",EDGE,{"derivedFrom":[makeQuery(id+"F6.boolean.opBoolean","MERGE",EDGE,{"derivedFrom":[subQ0,makeQuery(id+"F6.opPattern","COPY",EDGE,{"derivedFrom":subQ0,"instanceName":"1"})]}),makeQuery(id+"F13.opExtrude","SWEPT_EDGE",EDGE,{"disambiguationData":[OSD([sQuery(id+"F12.wireOp",EDGE,"E10.top"),sQuery(id+"F12.wireOp",EDGE,"E10.left")])]})]});}
            var Q1;
            Q1=makeQuery(id+"F6.opPattern","COPY",EDGE,{"derivedFrom":makeQuery(id+"F1.opExtrude","SWEPT_EDGE",EDGE,{"disambiguationData":[OSD([sQuery(id+"F0.wireOp",EDGE,"E0.top"),sQuery(id+"F0.wireOp",EDGE,"E0.left")])]}),"instanceName":"1"});
            var Q2;
            Q2=makeQuery(id+"F6.opPattern","COPY",EDGE,{"derivedFrom":makeQuery(id+"F1.opExtrude","SWEPT_EDGE",EDGE,{"disambiguationData":[OSD([sQuery(id+"F0.wireOp",EDGE,"E0.bottom"),sQuery(id+"F0.wireOp",EDGE,"E0.left")])]}),"instanceName":"1"});
            var Q3;
            {var subQ0=makeQuery(id+"F1.opExtrude","CAP_EDGE",EDGE,{"disambiguationData":[OSD([sQuery(id+"F0.wireOp",EDGE,"E0.bottom")])],"isStart":true});Q3=makeQuery(id+"F13.boolean.opBoolean","MERGE",EDGE,{"derivedFrom":[makeQuery(id+"F6.boolean.opBoolean","MERGE",EDGE,{"derivedFrom":[subQ0,makeQuery(id+"F6.opPattern","COPY",EDGE,{"derivedFrom":subQ0,"instanceName":"1"})]}),makeQuery(id+"F13.opExtrude","SWEPT_EDGE",EDGE,{"disambiguationData":[OSD([sQuery(id+"F12.wireOp",EDGE,"E9.top"),sQuery(id+"F12.wireOp",EDGE,"E9.left")])]})]});}
            var Q4;
            {var subQ0=sQuery(id+"F0.wireOp",EDGE,"E0.top");var subQ1=makeQuery(id+"F1.opExtrude","SWEPT_FACE",FACE,{"disambiguationData":[OSD([subQ0])]});var subQ2=sQuery(id+"F0.wireOp",EDGE,"E0.left");Q4=makeQuery(id+"F15.boolean.opBoolean","SPLIT",EDGE,{"disambiguationData":[TD([subQ1])],"derivedFrom":makeQuery(id+"F6.opPattern","COPY",EDGE,{"derivedFrom":makeQuery(id+"F1.opExtrude","CAP_EDGE",EDGE,{"disambiguationData":[OSD([subQ2])],"isStart":true}),"instanceName":"1"})});}
            var Q5;
            {var subQ0=sQuery(id+"F0.wireOp",EDGE,"E0.left");var subQ1=sQuery(id+"F0.wireOp",EDGE,"E0.bottom");var subQ3=makeQuery(id+"F1.opExtrude","SWEPT_FACE",FACE,{"disambiguationData":[OSD([subQ1])]});Q5=makeQuery(id+"F15.boolean.opBoolean","SPLIT",EDGE,{"disambiguationData":[TD([subQ3])],"derivedFrom":makeQuery(id+"F6.opPattern","COPY",EDGE,{"derivedFrom":makeQuery(id+"F1.opExtrude","CAP_EDGE",EDGE,{"disambiguationData":[OSD([subQ0])],"isStart":true}),"instanceName":"1"})});}
            var Q6;
            Q6=makeQuery(id+"F1.opExtrude","CAP_EDGE",EDGE,{"disambiguationData":[OSD([sQuery(id+"F0.wireOp",EDGE,"E0.left")])],"isStart":true});
            chamfer(context, id + "F41", {"entities" : qUnion([Q0, Q1, Q2, Q3, Q4, Q5, Q6]), "width" : 0.5 * mm, "tangentPropagation" : true});
        }
        {
            var Q0;
            Q0=makeQuery(id+"F22.opExtrude","SWEPT_BODY",BODY,{"disambiguationData":[OSD([sQuery(id+"F21.wireOp",EDGE,"E13.bottom"),sQuery(id+"F21.wireOp",EDGE,"E13.top"),sQuery(id+"F21.wireOp",EDGE,"E13.left"),sQuery(id+"F21.wireOp",EDGE,"E13.right")])]});
            transform(context, id + "F42", {"entities" : qUnion([Q0]), "transformType" : TransformType.TRANSLATION_3D, "dx" : 50 * mm, "dy" : 0 * mm, "dz" : 0 * mm, "makeCopy" : true});
        }
        {
            var Q0;
            Q0=makeQuery(id+"F42.opPattern","COPY",BODY,{"derivedFrom":makeQuery(id+"F22.opExtrude","SWEPT_BODY",BODY,{"disambiguationData":[OSD([sQuery(id+"F21.wireOp",EDGE,"E13.bottom"),sQuery(id+"F21.wireOp",EDGE,"E13.top"),sQuery(id+"F21.wireOp",EDGE,"E13.left"),sQuery(id+"F21.wireOp",EDGE,"E13.right")])]}),"instanceName":"1"});
            transform(context, id + "F43", {"entities" : qUnion([Q0]), "transformType" : TransformType.TRANSLATION_3D, "dx" : 50 * mm, "dy" : 0 * mm, "dz" : 0 * mm, "makeCopy" : true});
        }
        {
            var Q0;
            Q0=makeQuery(id+"F42.opPattern","COPY",FACE,{"derivedFrom":makeQuery(id+"F24.boolean.opBoolean","MERGE",FACE,{"derivedFrom":[makeQuery(id+"F22.opExtrude","SWEPT_FACE",FACE,{"disambiguationData":[OSD([sQuery(id+"F21.wireOp",EDGE,"E13.top")])]}),makeQuery(id+"F24.opExtrude","SWEPT_FACE",FACE,{"disambiguationData":[OSD([sQuery(id+"F23.wireOp",EDGE,"E14.top")])]})]}),"instanceName":"1"});
            var sketch = newSketch(context, id + "F44", { "sketchPlane" : qUnion([Q0])});
            skLineSegment(sketch, "E28.bottom", {"start": v(110, 5) * mm, "end": v(98.17, 5) * mm});
            skLineSegment(sketch, "E28.top", {"start": v(110, 11.38) * mm, "end": v(98.17, 11.38) * mm});
            skLineSegment(sketch, "E28.left", {"start": v(110, 5) * mm, "end": v(110, 11.38) * mm});
            skLineSegment(sketch, "E28.right", {"start": v(98.17, 5) * mm, "end": v(98.17, 11.38) * mm});
            skLineSegment(sketch, "E29.bottom", {"start": v(110, -4.9) * mm, "end": v(95.62, -4.9) * mm});
            skLineSegment(sketch, "E29.top", {"start": v(110, -10.4) * mm, "end": v(95.62, -10.4) * mm});
            skLineSegment(sketch, "E29.left", {"start": v(110, -4.9) * mm, "end": v(110, -10.4) * mm});
            skLineSegment(sketch, "E29.right", {"start": v(95.62, -4.9) * mm, "end": v(95.62, -10.4) * mm});
            skSolve(sketch);
        }
        {
            var Q0;
            Q0 = qSketchRegion(id + "F44", true);
            extrude(context, id + "F45", {"entities" : qUnion([Q0]), "operationType" : NewBodyOperationType.REMOVE, "oppositeDirection" : true, "depth" : 25 * mm, "offsetDistance" : 25 * mm});
        }
        {
            var Q0;
            Q0=makeQuery(id+"F43.opPattern","COPY",FACE,{"derivedFrom":makeQuery(id+"F42.opPattern","COPY",FACE,{"derivedFrom":makeQuery(id+"F24.boolean.opBoolean","MERGE",FACE,{"derivedFrom":[makeQuery(id+"F22.opExtrude","SWEPT_FACE",FACE,{"disambiguationData":[OSD([sQuery(id+"F21.wireOp",EDGE,"E13.top")])]}),makeQuery(id+"F24.opExtrude","SWEPT_FACE",FACE,{"disambiguationData":[OSD([sQuery(id+"F23.wireOp",EDGE,"E14.top")])]})]}),"instanceName":"1"}),"instanceName":"1"});
            var sketch = newSketch(context, id + "F46", { "sketchPlane" : qUnion([Q0])});
            skLineSegment(sketch, "E30.bottom", {"start": v(160, -9) * mm, "end": v(170.56, -9) * mm});
            skLineSegment(sketch, "E30.top", {"start": v(160, 8.44) * mm, "end": v(170.56, 8.44) * mm});
            skLineSegment(sketch, "E30.left", {"start": v(160, -9) * mm, "end": v(160, 8.44) * mm});
            skLineSegment(sketch, "E30.right", {"start": v(170.56, -9) * mm, "end": v(170.56, 8.44) * mm});
            skSolve(sketch);
        }
        {
            var Q0;
            {var subQ10=sQuery(id+"F46.wireOp",EDGE,"E30.bottom");Q0=makeQuery(id+"F46.imprint","IMPRINT",FACE,{"disambiguationData":[TD([[makeQuery(id+"F46.imprint","IMPRINT",EDGE,{"derivedFrom":subQ10}),1.0]])]});}
            var Q1;
            {var subQ1=sQuery(id+"F23.wireOp",EDGE,"E14.top");var subQ2=sQuery(id+"F21.wireOp",EDGE,"E13.top");var subQ3=makeQuery(id+"F43.opPattern","COPY",EDGE,{"derivedFrom":makeQuery(id+"F42.opPattern","COPY",EDGE,{"derivedFrom":makeQuery(id+"F24.opExtrude","SWEPT_EDGE",EDGE,{"disambiguationData":[OSD([subQ2,subQ1,sQuery(id+"F23.wireOp",EDGE,"E14.right")])]}),"instanceName":"1"}),"instanceName":"1"});Q1=makeQuery(id+"F46.imprint","IMPRINT",FACE,{"disambiguationData":[TD([[makeQuery(id+"F46.imprint","IMPRINT",EDGE,{"derivedFrom":subQ3}),1.0]])]});}
            extrude(context, id + "F47", {"entities" : qUnion([Q0, Q1]), "operationType" : NewBodyOperationType.REMOVE, "oppositeDirection" : true, "depth" : 25 * mm, "offsetDistance" : 25 * mm});
        }
        {
            var Q0;
            Q0=makeQuery(id+"F45.boolean.opBoolean","MERGE",FACE,{"derivedFrom":[makeQuery(id+"F42.opPattern","COPY",FACE,{"derivedFrom":makeQuery(id+"F29.boolean.opBoolean","COPY",FACE,{"derivedFrom":makeQuery(id+"F29.opExtrude","CAP_FACE",FACE,{"disambiguationData":[OSD([sQuery(id+"F23.wireOp",EDGE,"E14.left")])],"isStart":false})}),"instanceName":"1"}),makeQuery(id+"F45.opExtrude","SWEPT_FACE",FACE,{"disambiguationData":[OSD([sQuery(id+"F44.wireOp",EDGE,"E29.bottom")])]})]});
            var sketch = newSketch(context, id + "F48", { "sketchPlane" : qUnion([Q0])});
            skLineSegment(sketch, "E31.bottom", {"start": v(105, 2.5) * mm, "end": v(110, 2.5) * mm});
            skLineSegment(sketch, "E31.top", {"start": v(105, 5) * mm, "end": v(110, 5) * mm});
            skLineSegment(sketch, "E31.left", {"start": v(105, 2.5) * mm, "end": v(105, 5) * mm});
            skLineSegment(sketch, "E31.right", {"start": v(110, 2.5) * mm, "end": v(110, 5) * mm});
            skSolve(sketch);
        }
        {
            var Q0;
            {var subQ5=sQuery(id+"F48.wireOp",EDGE,"E31.bottom");Q0=makeQuery(id+"F48.imprint","IMPRINT",FACE,{"disambiguationData":[TD([[makeQuery(id+"F48.imprint","IMPRINT",EDGE,{"derivedFrom":subQ5}),1.0]])]});}
            extrude(context, id + "F49", {"entities" : qUnion([Q0]), "operationType" : NewBodyOperationType.REMOVE, "oppositeDirection" : true, "depth" : 25 * mm, "offsetDistance" : 25 * mm});
        }
        {
            var Q0;
            {var subQ1=sQuery(id+"F21.wireOp",EDGE,"E13.top");var subQ3=sQuery(id+"F21.wireOp",EDGE,"E13.right");var subQ4=sQuery(id+"F21.wireOp",EDGE,"E13.bottom");var subQ7=sQuery(id+"F21.wireOp",EDGE,"E13.left");var subQ8=makeQuery(id+"F22.opExtrude","CAP_FACE",FACE,{"disambiguationData":[OSD([subQ4,subQ1,subQ7,subQ3])],"isStart":false});var subQ9=sQuery(id+"F23.wireOp",EDGE,"E14.left");Q0=makeQuery(id+"F47.boolean.opBoolean","MERGE",FACE,{"derivedFrom":[makeQuery(id+"F43.opPattern","COPY",FACE,{"derivedFrom":makeQuery(id+"F42.opPattern","COPY",FACE,{"derivedFrom":makeQuery(id+"F29.boolean.opBoolean","MERGE",FACE,{"derivedFrom":[makeQuery(id+"F24.boolean.opBoolean","SPLIT",FACE,{"disambiguationData":[TD([makeQuery(id+"F22.opExtrude","SWEPT_FACE",FACE,{"disambiguationData":[OSD([subQ7])]})])],"derivedFrom":subQ8}),makeQuery(id+"F29.opExtrude","SWEPT_FACE",FACE,{"disambiguationData":[OSD([subQ9])]})]}),"instanceName":"1"}),"instanceName":"1"}),makeQuery(id+"F43.opPattern","COPY",FACE,{"derivedFrom":makeQuery(id+"F42.opPattern","COPY",FACE,{"derivedFrom":makeQuery(id+"F24.boolean.opBoolean","SPLIT",FACE,{"disambiguationData":[TD([makeQuery(id+"F22.opExtrude","SWEPT_FACE",FACE,{"disambiguationData":[OSD([subQ3])]})])],"derivedFrom":subQ8}),"instanceName":"1"}),"instanceName":"1"}),makeQuery(id+"F47.opExtrude","SWEPT_FACE",FACE,{"disambiguationData":[OSD([sQuery(id+"F46.wireOp",EDGE,"E30.left")])]})]});}
            var sketch = newSketch(context, id + "F50", { "sketchPlane" : qUnion([Q0])});
            skLineSegment(sketch, "E32.bottom", {"start": v(-5, 5) * mm, "end": v(5, 5) * mm});
            skLineSegment(sketch, "E32.top", {"start": v(-5, 2.4) * mm, "end": v(5, 2.4) * mm});
            skLineSegment(sketch, "E32.left", {"start": v(-5, 5) * mm, "end": v(-5, 2.4) * mm});
            skLineSegment(sketch, "E32.right", {"start": v(5, 5) * mm, "end": v(5, 2.4) * mm});
            skSolve(sketch);
        }
        {
            var Q0;
            Q0=makeQuery(id+"F50.imprint","IMPRINT",FACE,{"disambiguationData":[TD([[makeQuery(id+"F50.imprint","IMPRINT",EDGE,{"derivedFrom":sQuery(id+"F50.wireOp",EDGE,"E32.bottom")}),-1.0]])]});
            extrude(context, id + "F51", {"entities" : qUnion([Q0]), "operationType" : NewBodyOperationType.REMOVE, "oppositeDirection" : true, "depth" : 25 * mm, "offsetDistance" : 25 * mm});
        }
        {
            var Q0;
            Q0=makeQuery(id+"F49.boolean.opBoolean","COPY",FACE,{"derivedFrom":makeQuery(id+"F49.opExtrude","SWEPT_FACE",FACE,{"disambiguationData":[OSD([sQuery(id+"F48.wireOp",EDGE,"E31.bottom")])]})});
            var sketch = newSketch(context, id + "F52", { "sketchPlane" : qUnion([Q0])});
            skCircle(sketch, "E33", {"center": v(107.5, 0.05) * mm, "radius": 1.5 * mm});
            skCircle(sketch, "E34", {"center": v(157.5, 0) * mm, "radius": 1.5 * mm});
            skSolve(sketch);
        }
        {
            var Q0;
            Q0 = qSketchRegion(id + "F52", true);
            extrude(context, id + "F53", {"entities" : qUnion([Q0]), "operationType" : NewBodyOperationType.REMOVE, "oppositeDirection" : true, "depth" : 25 * mm, "offsetDistance" : 25 * mm});
        }
    });
